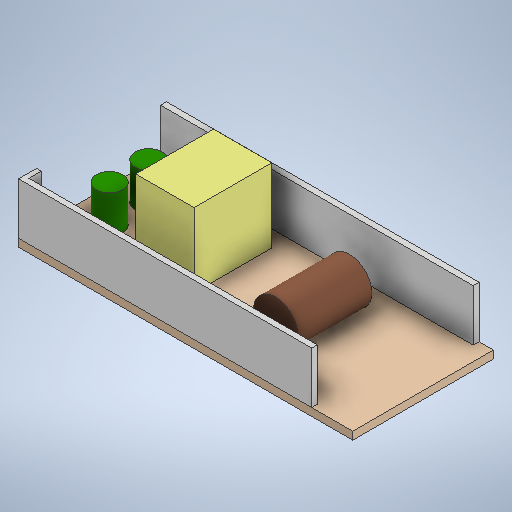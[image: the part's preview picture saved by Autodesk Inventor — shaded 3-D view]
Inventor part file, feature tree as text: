
AUTODESK INVENTOR PART (.ipt)
format: ipt  version: 2025 (Build 290162000, 162)  size: 287,232 bytes
history: native  units: in
note: dims shown in document units (in); Inventor stores cm internally (conversion verified against a paired STEP export)
features: extrude x5, sketch x5, projected_geometry x3, plane x1
ambient origin geometry x8: Origin, YZ Plane, XZ Plane, XY Plane, X Axis, Y Axis, Z Axis, Center Point
bodies: Solid1 (feature_tree), Solid2 (feature_tree)
feature tree (14):
  extrude  "Extrusion1"  Depth=1.81in
  extrude  "Extrusion2"  Depth=0.6625in TaperAngle=0.0deg
  extrude  "Extrusion3"  Depth=0.75in
  extrude  "Extrusion4"  Depth=0.95in TaperAngle=0.0deg
  plane  "Work Plane1"
  extrude  "Extrusion5"  [1 undecoded]
  sketch  "Sketch1"  dims[d0=4.3in d1=1.81in]
  sketch  "Sketch2"  dims[d2=0.1in d3=0.0in d4=0.6625in d5=0.0in]
  projected_geometry  "Projected Loop1"
  sketch  "Sketch3"  dims[d6=0.475in d7=0.0in d8=0.75in]
  sketch  "Sketch4"  dims[d9=1.0in d10=0.95in d11=0.0in]
  projected_geometry  "Projected Loop2"
  sketch  "Sketch5"  dims[d12=0.95in d13=0.0in]
  projected_geometry  "Projected Loop3"
note: 1 required parameter value undecoded (feature->parameter linkage not recoverable at this tier; creation-order binding heuristic only, values carry confidence <= 0.55)
